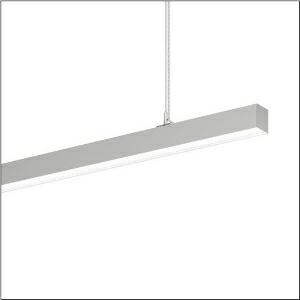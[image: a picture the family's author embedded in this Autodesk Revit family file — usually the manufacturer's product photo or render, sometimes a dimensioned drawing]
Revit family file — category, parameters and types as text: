
# Revit family: silica_r__21_51mx30da44sb_e9ec
name_source: partatom
category: Lighting Fixtures
units: mm (PartAtom-declared; Revit-internal decimal feet)

## family parameters
Cut with Voids When Loaded = No
Host = Face
Light Source = No
Part Type = Normal
Room Calculation Point = No
Round Connector Dimension = Use Diameter
Shared = No

## types (1)
- --- (1 x LED, 4210 lm, 26 W, 4000K)
    Apparent Load = 26 VA
    CIE Flux Codes = 47 79 96 57 100
    Color Rendering = 80
    Color Temperature = 4000K
    Default Elevation = 1800 mm
    Description = Silica® 21, office luminaire, primary optical cover: cover, of PMMA, opal, light emission: direct/indirect distribution, primary light characteristic: symmetric, installation type: suspended mounting, LED, rated luminous flux: 4.210lm, luminous efficacy: 162lm/W, light colour: 840, colour temperature: 4000K, with terminal, 3+2-pole, max. 2.5mm², mains connection: 220..240V, AC, 50/60Hz, rated input power: 26W, luminaire housing, of aluminium, metallic grey (RAL 9006), length: 1.204mm, width: 53mm, height: 53mm, protection rating (complete): IP20, insulation class (complete): insulation class I (protective earthing), certification: CE, permissible operating ambient temperature: 0..+35°C, standard: EN 50419, packaging unit: 1 piece
    Height = 53 mm
    Lamp = 1 x LED
    Lamp Light Flux = 4210 lm
    Lamp Power = 26 W
    Lamp count = 1
    Length = 1204 mm
    Luminous efficacy = 162 lm/W
    Manufacturer = Siteco
    ModVariant = No
    Model = 51MX30DA44SB
    Mounting Place = Ceiling
    Mounting Type = Pendant
    Number of Poles = 1
    OnlyDefault = Yes
    Power Factor = 1
    Product Name = Silica® 21
    Product group = office luminaire | ceiling pendant
    ProductGroupID = 905
    Protection Class = Protection class I
    Protection Degree = IP 20
    RLX_Detail_Level = 1
    RlxData = <blob elided: 23129 chars, md5=1c0df7aa>
    Socket = socket
    Standby Power = 0 W
    System Light Flux = 4210 lm
    System Power = 26 W
    Type Comments = factory setting: luminous flux: 100 % | dim-lin: 254 | 218 mA
    Type Image = l_1251727.jpg
    URL = http://relux.com
    VarID = @adj_025589
    Voltage = 0 V
    Weight = 0.00 kg
    Width = 53 mm

## geometry (parser evidence)
native form markers: Blend x4, Sweep x15
no freeform markers — native parametric forms only
